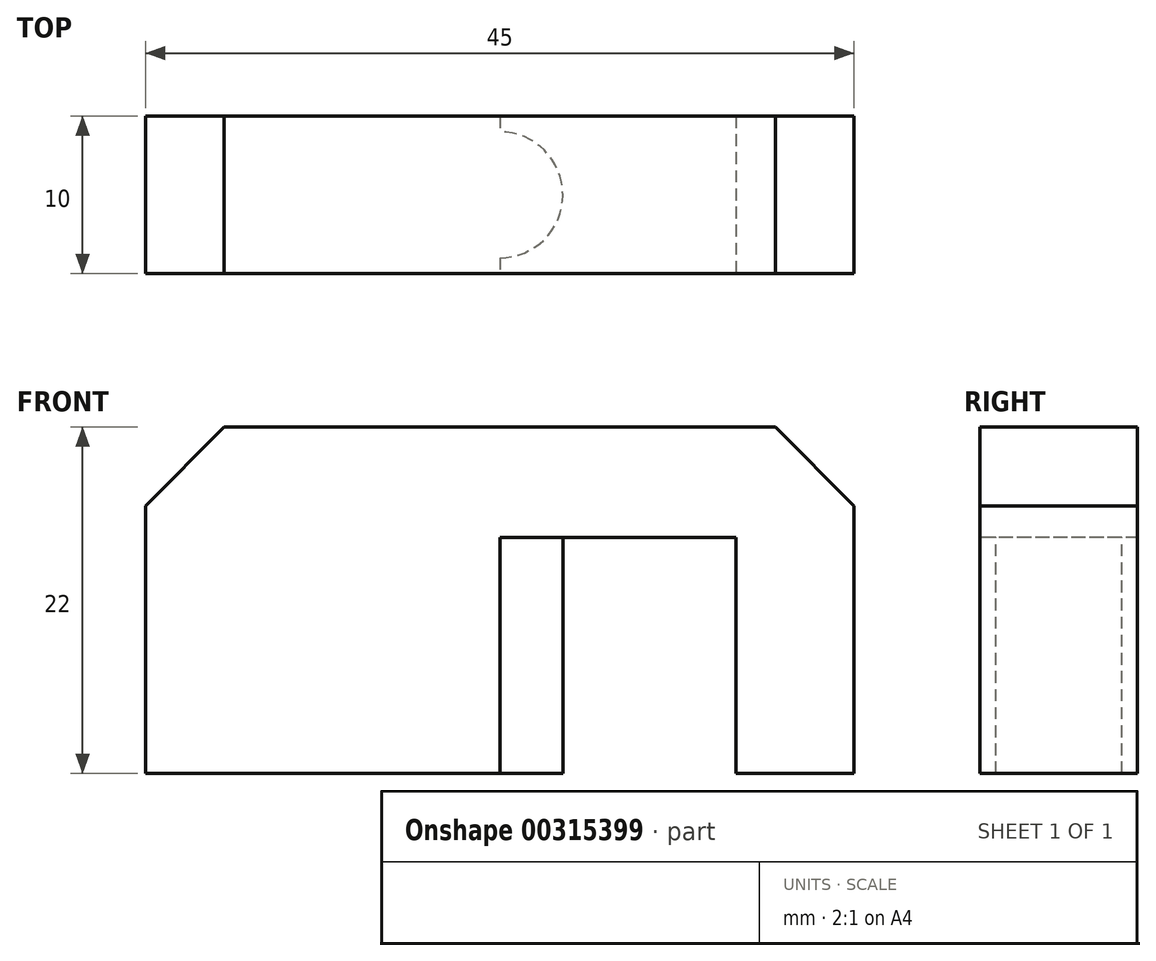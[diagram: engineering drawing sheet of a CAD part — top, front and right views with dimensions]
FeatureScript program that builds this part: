
annotation { "Feature Type Name" : "Feature", "Feature Type Description" : "" }
export const myFeature = defineFeature(function(context is Context, id is Id, definition is map)
    precondition{}
    {
        {
            var Q0;
            Q0=qCreatedBy(makeId("Front.planeOp"),FACE);
            var sketch = newSketch(context, id + "F0", { "sketchPlane" : qUnion([Q0])});
            skLineSegment(sketch, "E0.bottom", {"start": v(-19.91, 11) * mm, "end": v(25.09, 11) * mm});
            skLineSegment(sketch, "E0.top", {"start": v(-19.91, -11) * mm, "end": v(25.09, -11) * mm});
            skLineSegment(sketch, "E0.left", {"start": v(-19.91, 11) * mm, "end": v(-19.91, -11) * mm});
            skLineSegment(sketch, "E0.right", {"start": v(25.09, 11) * mm, "end": v(25.09, -11) * mm});
            skPoint(sketch, "E0.middle", {"position": v(2.59, 0) * mm});
            skSolve(sketch);
        }
        {
            var Q0;
            Q0=makeQuery(id+"F0.imprint","IMPRINT",FACE,{"disambiguationData":[TD([[makeQuery(id+"F0.imprint","IMPRINT",EDGE,{"derivedFrom":sQuery(id+"F0.wireOp",EDGE,"E0.bottom")}),-1.0]])]});
            extrude(context, id + "F1", {"entities" : qUnion([Q0]), "depth" : 10 * mm});
        }
        {
            var Q0;
            Q0=makeQuery(id+"F1.opExtrude","CAP_FACE",FACE,{"disambiguationData":[OSD([sQuery(id+"F0.wireOp",EDGE,"E0.bottom"),sQuery(id+"F0.wireOp",EDGE,"E0.top"),sQuery(id+"F0.wireOp",EDGE,"E0.left"),sQuery(id+"F0.wireOp",EDGE,"E0.right")])],"isStart":false});
            var sketch = newSketch(context, id + "F2", { "sketchPlane" : qUnion([Q0])});
            skLineSegment(sketch, "E1.0.0", {"start": v(-19.91, 11) * mm, "end": v(-19.91, -11) * mm});
            skLineSegment(sketch, "E1.0.1", {"start": v(-19.91, -11) * mm, "end": v(25.09, -11) * mm});
            skLineSegment(sketch, "E1.0.2", {"start": v(25.09, -11) * mm, "end": v(25.09, 11) * mm});
            skLineSegment(sketch, "E1.0.3", {"start": v(25.09, 11) * mm, "end": v(-19.91, 11) * mm});
            skLineSegment(sketch, "E2", {"start": v(2.59, 11) * mm, "end": v(2.59, -11) * mm, "construction": true});
            skLineSegment(sketch, "E3.bottom", {"start": v(2.59, -11) * mm, "end": v(-12.41, -11) * mm});
            skLineSegment(sketch, "E3.top", {"start": v(2.59, 4) * mm, "end": v(-12.41, 4) * mm});
            skLineSegment(sketch, "E3.left", {"start": v(2.59, -11) * mm, "end": v(2.59, 4) * mm});
            skLineSegment(sketch, "E3.right", {"start": v(-12.41, -11) * mm, "end": v(-12.41, 4) * mm});
            skLineSegment(sketch, "E4.MirrorCS", {"start": v(2.59, 4) * mm, "end": v(17.59, 4) * mm});
            skLineSegment(sketch, "E5.MirrorCS", {"start": v(17.59, -11) * mm, "end": v(17.59, 4) * mm});
            skSolve(sketch);
        }
        {
            var Q0;
            Q0=makeQuery(id+"F2.imprint","IMPRINT",FACE,{"disambiguationData":[TD([[makeQuery(id+"F2.imprint","IMPRINT",EDGE,{"derivedFrom":sQuery(id+"F2.wireOp",EDGE,"E3.bottom")}),1.0]])]});
            var Q1;
            {var subQ0=sQuery(id+"F2.wireOp",EDGE,"E3.left");Q1=makeQuery(id+"F2.imprint","IMPRINT",FACE,{"disambiguationData":[TD([[makeQuery(id+"F2.imprint","IMPRINT",EDGE,{"derivedFrom":subQ0}),-1.0]])]});}
            extrude(context, id + "F3", {"entities" : qUnion([Q0, Q1]), "operationType" : NewBodyOperationType.REMOVE, "oppositeDirection" : true, "depth" : 25 * mm});
        }
        {
            var Q0;
            Q0=makeQuery(id+"F1.opExtrude","SWEPT_EDGE",EDGE,{"disambiguationData":[OSD([sQuery(id+"F0.wireOp",EDGE,"E0.bottom"),sQuery(id+"F0.wireOp",EDGE,"E0.left")])]});
            var Q1;
            Q1=makeQuery(id+"F1.opExtrude","SWEPT_EDGE",EDGE,{"disambiguationData":[OSD([sQuery(id+"F0.wireOp",EDGE,"E0.bottom"),sQuery(id+"F0.wireOp",EDGE,"E0.right")])]});
            chamfer(context, id + "F4", {"entities" : qUnion([Q0, Q1]), "width" : 5 * mm, "tangentPropagation" : true});
        }
        {
            var Q0;
            Q0=makeQuery(id+"F3.boolean.opBoolean","COPY",FACE,{"derivedFrom":makeQuery(id+"F3.opExtrude","SWEPT_FACE",FACE,{"disambiguationData":[OSD([sQuery(id+"F2.wireOp",EDGE,"E3.top"),sQuery(id+"F2.wireOp",EDGE,"E4.MirrorCS")])]})});
            var sketch = newSketch(context, id + "F5", { "sketchPlane" : qUnion([Q0])});
            skLineSegment(sketch, "E6.0.0", {"start": v(17.59, 0) * mm, "end": v(17.59, 10) * mm});
            skLineSegment(sketch, "E6.0.1", {"start": v(17.59, 10) * mm, "end": v(-12.41, 10) * mm});
            skLineSegment(sketch, "E6.0.2", {"start": v(-12.41, 10) * mm, "end": v(-12.41, 0) * mm});
            skLineSegment(sketch, "E6.0.3", {"start": v(-12.41, 0) * mm, "end": v(17.59, 0) * mm});
            skLineSegment(sketch, "E7", {"start": v(2.59, 10) * mm, "end": v(2.59, 0) * mm, "construction": true});
            skCircle(sketch, "E8", {"center": v(2.59, 5) * mm, "radius": 4 * mm});
            skSolve(sketch);
        }
        {
            var Q0;
            Q0=makeQuery(id+"F5.imprint","IMPRINT",FACE,{"disambiguationData":[TD([[makeQuery(id+"F5.imprint","IMPRINT",EDGE,{"derivedFrom":sQuery(id+"F5.wireOp",EDGE,"E8")}),1.0]])]});
            var Q1;
            {var subQ1=sQuery(id+"F0.wireOp",EDGE,"E0.left");var subQ2=sQuery(id+"F0.wireOp",EDGE,"E0.top");Q1=makeQuery(id+"F3.boolean.opBoolean","SPLIT",FACE,{"disambiguationData":[TD([makeQuery(id+"F1.opExtrude","SWEPT_FACE",FACE,{"disambiguationData":[OSD([subQ1])]})])],"derivedFrom":makeQuery(id+"F1.opExtrude","SWEPT_FACE",FACE,{"disambiguationData":[OSD([subQ2])]})});}
            extrude(context, id + "F6", {"entities" : qUnion([Q0]), "operationType" : NewBodyOperationType.ADD, "endBound" : BoundingType.UP_TO_SURFACE, "endBoundEntityFace" : qUnion([Q1]), "depth" : 25 * mm});
        }
    });
